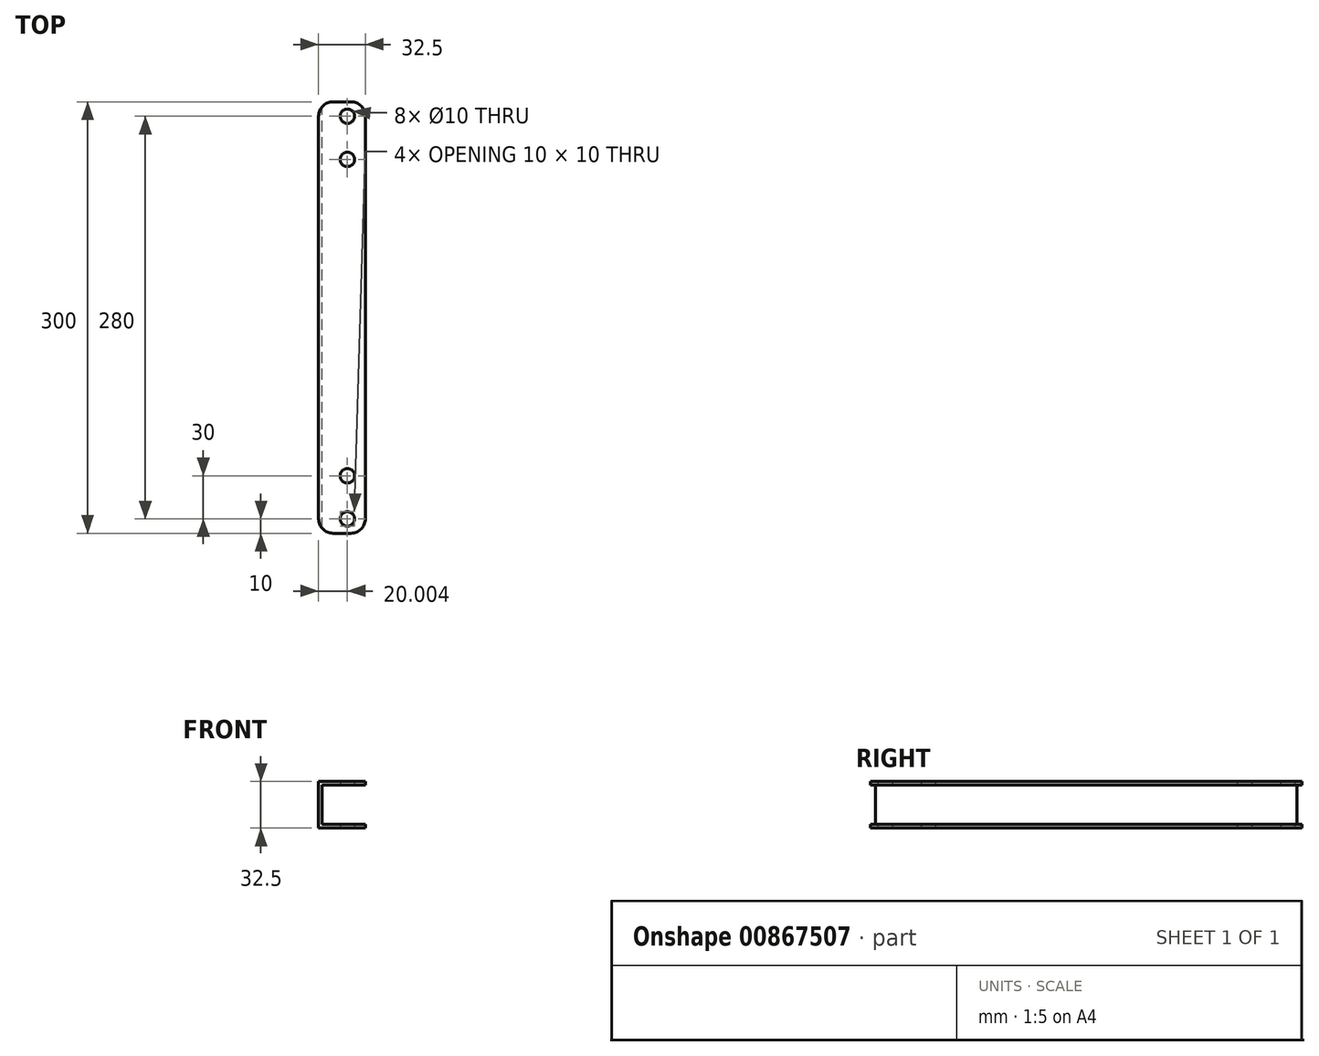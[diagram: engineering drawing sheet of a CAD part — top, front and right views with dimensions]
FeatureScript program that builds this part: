
annotation { "Feature Type Name" : "Feature", "Feature Type Description" : "" }
export const myFeature = defineFeature(function(context is Context, id is Id, definition is map)
    precondition{}
    {
        {
            var Q0;
            Q0=qCreatedBy(makeId("Front.planeOp"),FACE);
            var sketch = newSketch(context, id + "F0", { "sketchPlane" : qUnion([Q0])});
            skLineSegment(sketch, "E0.bottom", {"start": v(-74.99, 0) * mm, "end": v(-42.49, 0) * mm});
            skLineSegment(sketch, "E0.top", {"start": v(-74.99, 32.5) * mm, "end": v(-42.49, 32.5) * mm});
            skLineSegment(sketch, "E0.left", {"start": v(-74.99, 0) * mm, "end": v(-74.99, 32.5) * mm});
            skLineSegment(sketch, "E0.right", {"start": v(-42.49, 0) * mm, "end": v(-42.49, 2.5) * mm});
            skLineSegment(sketch, "E1.top", {"start": v(-42.49, 2.5) * mm, "end": v(-72.49, 2.5) * mm});
            skLineSegment(sketch, "E2.top", {"start": v(-42.49, 30) * mm, "end": v(-72.49, 30) * mm});
            skLineSegment(sketch, "E3.trimOffspring", {"start": v(-42.49, 30) * mm, "end": v(-42.49, 32.5) * mm});
            skPoint(sketch, "E2.left.start.orphan", {"position": v(-42.49, 16.25) * mm});
            skLineSegment(sketch, "E4", {"start": v(-72.49, 30) * mm, "end": v(-72.49, 2.5) * mm});
            skSolve(sketch);
        }
        {
            var Q0;
            Q0=qCreatedBy(makeId("Top.planeOp"),FACE);
            var sketch = newSketch(context, id + "F1", { "sketchPlane" : qUnion([Q0])});
            skLineSegment(sketch, "E5.0", {"start": v(0, -150) * mm, "end": v(-82.52, -150) * mm, "construction": true});
            skLineSegment(sketch, "E6.bottom", {"start": v(-59.99, -290) * mm, "end": v(-54.99, -290) * mm});
            skCircle(sketch, "E7", {"center": v(-54.99, -10) * mm, "radius": 5 * mm});
            skCircle(sketch, "E8", {"center": v(-54.99, -290) * mm, "radius": 5 * mm});
            skCircle(sketch, "E9", {"center": v(-54.99, -260) * mm, "radius": 5 * mm});
            skCircle(sketch, "E10", {"center": v(-54.99, -40) * mm, "radius": 5 * mm});
            skSolve(sketch);
        }
        {
            var Q0;
            Q0=makeQuery(id+"F0.imprint","IMPRINT",FACE,{"disambiguationData":[TD([[makeQuery(id+"F0.imprint","IMPRINT",EDGE,{"derivedFrom":sQuery(id+"F0.wireOp",EDGE,"E0.bottom")}),1.0]])]});
            extrude(context, id + "F2", {"entities" : qUnion([Q0]), "depth" : 300 * mm, "offsetDistance" : 25 * mm});
        }
        {
            var Q0;
            {var subQ0=sQuery(id+"F1.wireOp",EDGE,"E8");Q0=makeQuery(id+"F1.imprint","IMPRINT",FACE,{"disambiguationData":[TD([[makeQuery(id+"F1.imprint","IMPRINT",EDGE,{"disambiguationData":[TD([[makeQuery(id+"F1.imprint","IMPRINT",VERTEX,{"derivedFrom":subQ0}),-1.0]])],"derivedFrom":subQ0}),1.0]])]});}
            var Q1;
            Q1=makeQuery(id+"F1.imprint","IMPRINT",FACE,{"disambiguationData":[TD([[makeQuery(id+"F1.imprint","IMPRINT",EDGE,{"derivedFrom":sQuery(id+"F1.wireOp",EDGE,"E9")}),1.0]])]});
            var Q2;
            Q2=makeQuery(id+"F1.imprint","IMPRINT",FACE,{"disambiguationData":[TD([[makeQuery(id+"F1.imprint","IMPRINT",EDGE,{"derivedFrom":sQuery(id+"F1.wireOp",EDGE,"E10")}),1.0]])]});
            var Q3;
            Q3=makeQuery(id+"F1.imprint","IMPRINT",FACE,{"disambiguationData":[TD([[makeQuery(id+"F1.imprint","IMPRINT",EDGE,{"derivedFrom":sQuery(id+"F1.wireOp",EDGE,"E7")}),1.0]])]});
            extrude(context, id + "F3", {"entities" : qUnion([Q0, Q1, Q2, Q3]), "operationType" : NewBodyOperationType.REMOVE, "depth" : 46 * mm, "offsetDistance" : 25 * mm});
        }
        {
            var Q0;
            Q0=makeQuery(id+"F2.opExtrude","CAP_EDGE",EDGE,{"disambiguationData":[OSD([sQuery(id+"F0.wireOp",EDGE,"E0.right")])],"isStart":true});
            var Q1;
            Q1=makeQuery(id+"F2.opExtrude","CAP_EDGE",EDGE,{"disambiguationData":[OSD([sQuery(id+"F0.wireOp",EDGE,"E3.trimOffspring")])],"isStart":true});
            var Q2;
            Q2=makeQuery(id+"F2.opExtrude","CAP_EDGE",EDGE,{"disambiguationData":[OSD([sQuery(id+"F0.wireOp",EDGE,"E3.trimOffspring")])],"isStart":false});
            var Q3;
            Q3=makeQuery(id+"F2.opExtrude","CAP_EDGE",EDGE,{"disambiguationData":[OSD([sQuery(id+"F0.wireOp",EDGE,"E0.right")])],"isStart":false});
            var Q4;
            Q4=makeQuery(id+"F2.opExtrude","CAP_EDGE",EDGE,{"disambiguationData":[OSD([sQuery(id+"F0.wireOp",EDGE,"E0.left")])],"isStart":true});
            var Q5;
            Q5=makeQuery(id+"F2.opExtrude","CAP_EDGE",EDGE,{"disambiguationData":[OSD([sQuery(id+"F0.wireOp",EDGE,"E0.left")])],"isStart":false});
            fillet(context, id + "F4", {"entities" : qUnion([Q0, Q1, Q2, Q3, Q4, Q5]), "radius" : 10 * mm, "tangentPropagation" : true, "allowEdgeOverflow" : false});
        }
    });
